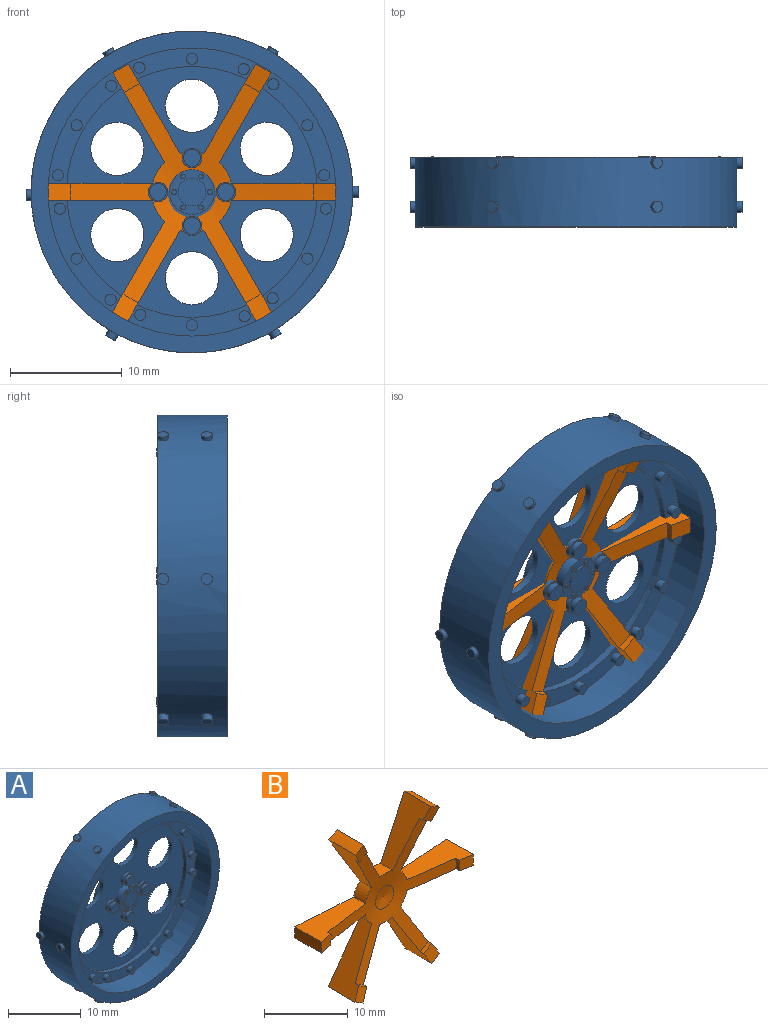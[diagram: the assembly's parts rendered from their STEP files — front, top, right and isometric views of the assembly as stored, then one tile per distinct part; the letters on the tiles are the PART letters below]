
ASSEMBLY  parts=2 mates=1
PART A: 117 faces, bbox 29.7x6.2x28.8 mm
  f0: cylinder r=14.39mm len=28.78mm, axis (0,1,0), area 551.2mm2, adj f1,f5,f87,f90,f92,f95,f97,f100
  f1: plane 28.78x28.78mm, normal (0,1,0), area 128.3mm2, adj f0,f3,f87,f88,f92,f93,f97,f98
  f2: plane 22.45x22.45mm, normal (0,-1,0), area 267.2mm2, adj f6,f9,f13,f17,f21,f25,f41,f42
  f3: cylinder r=12.89mm len=25.78mm, axis (0,1,0), area 137.7mm2, adj f1,f8
  f4: cylinder r=12.89mm len=25.78mm, axis (0,1,0), area 259.2mm2, adj f5,f7
  f5: plane 28.78x28.78mm, normal (0,-1,0), area 128.6mm2, adj f0,f4
  f6: cylinder r=11.22mm len=22.45mm, axis (0,1,0), area 45.8mm2, adj f2,f7
  f7: plane 25.78x25.78mm, normal (0,-1,0), area 112.1mm2, adj f4,f6,f47,f49,f51,f53,f55,f57
  f8: plane 25.78x25.78mm, normal (0,1,0), area 370.3mm2, adj f3,f41,f42,f43,f44,f45,f46,f84
  f9: cylinder r=0.88mm len=1.75mm, axis (0,1,0), area 2.7mm2, adj f2,f10
  f10: plane 1.75x1.75mm, normal (0,-1,0), area 0.6mm2, adj f9,f12
  f11: plane 1.5x1.5mm, normal (0,-1,0), area 1.8mm2, adj f12
  f12: cylinder r=0.75mm len=1.5mm, axis (0,1,0), area 2.8mm2, adj f10,f11
  f13: cylinder r=0.88mm len=1.75mm, axis (0,1,0), area 2.7mm2, adj f2,f14
  f14: plane 1.75x1.75mm, normal (0,-1,0), area 0.6mm2, adj f13,f16
  f15: plane 1.5x1.5mm, normal (0,-1,0), area 1.8mm2, adj f16
  f16: cylinder r=0.75mm len=1.5mm, axis (0,1,0), area 2.8mm2, adj f14,f15
  f17: cylinder r=0.88mm len=1.75mm, axis (0,1,0), area 2.7mm2, adj f2,f18
  f18: plane 1.75x1.75mm, normal (0,-1,0), area 0.6mm2, adj f17,f20
  f19: plane 1.5x1.5mm, normal (0,-1,0), area 1.8mm2, adj f20
  f20: cylinder r=0.75mm len=1.5mm, axis (0,1,0), area 2.8mm2, adj f18,f19
  f21: cylinder r=0.88mm len=1.75mm, axis (0,1,0), area 2.7mm2, adj f2,f22
  f22: plane 1.75x1.75mm, normal (0,-1,0), area 0.6mm2, adj f21,f24
  f23: plane 1.5x1.5mm, normal (0,-1,0), area 1.8mm2, adj f24
  f24: cylinder r=0.75mm len=1.5mm, axis (0,1,0), area 2.8mm2, adj f22,f23
  f25: cylinder r=2mm len=4mm, axis (0,1,0), area 11.3mm2, adj f2,f26
  f26: plane 4x4mm, normal (0,-1,0), area 6.8mm2, adj f25,f28,f30,f32,f34,f36,f38,f40
  f27: plane 0.44x0.44mm, normal (0,-1,0), area 0.1mm2, adj f28
  f28: cylinder r=0.22mm len=0.44mm, axis (0,1,0), area 0.3mm2, adj f26,f27
  f29: plane 0.44x0.44mm, normal (0,-1,0), area 0.1mm2, adj f30
  f30: cylinder r=0.22mm len=0.44mm, axis (0,1,0), area 0.3mm2, adj f26,f29
  f31: plane 0.44x0.44mm, normal (0,-1,0), area 0.1mm2, adj f32
  f32: cylinder r=0.22mm len=0.44mm, axis (0,1,0), area 0.3mm2, adj f26,f31
  f33: plane 0.44x0.44mm, normal (0,-1,0), area 0.1mm2, adj f34
  f34: cylinder r=0.22mm len=0.44mm, axis (0,1,0), area 0.3mm2, adj f26,f33
  f35: plane 0.44x0.44mm, normal (0,-1,0), area 0.1mm2, adj f36
  f36: cylinder r=0.22mm len=0.44mm, axis (0,1,0), area 0.3mm2, adj f26,f35
  f37: plane 2.5x2.5mm, normal (0,-1,0), area 4.9mm2, adj f38
  f38: cylinder r=1.25mm len=2.5mm, axis (0,1,0), area 1.6mm2, adj f26,f37
  f39: plane 0.44x0.44mm, normal (0,-1,0), area 0.1mm2, adj f40
  f40: cylinder r=0.22mm len=0.44mm, axis (0,1,0), area 0.3mm2, adj f26,f39
  f41: cylinder r=2.38mm len=4.75mm, axis (0,-1,0), area 9.7mm2, adj f2,f8
  f42: cylinder r=2.38mm len=4.75mm, axis (0,-1,0), area 9.7mm2, adj f2,f8
  f43: cylinder r=2.38mm len=4.75mm, axis (0,-1,0), area 9.7mm2, adj f2,f8
  f44: cylinder r=2.38mm len=4.75mm, axis (0,-1,0), area 9.7mm2, adj f2,f8
  f45: cylinder r=2.38mm len=4.75mm, axis (0,-1,0), area 9.7mm2, adj f2,f8
  f46: cylinder r=2.38mm len=4.75mm, axis (0,-1,0), area 9.7mm2, adj f2,f8
  f47: cylinder r=0.5mm len=1mm, axis (0,1,0), area 2.4mm2, adj f7,f48
  f48: plane 1x1mm, normal (0,-1,0), area 0.8mm2, adj f47
  f49: cylinder r=0.5mm len=1mm, axis (0,1,0), area 2.4mm2, adj f7,f50
  f50: plane 1x1mm, normal (0,-1,0), area 0.8mm2, adj f49
  f51: cylinder r=0.5mm len=1mm, axis (0,1,0), area 2.4mm2, adj f7,f52
  f52: plane 1x1mm, normal (0,-1,0), area 0.8mm2, adj f51
  f53: cylinder r=0.5mm len=1mm, axis (0,1,0), area 2.4mm2, adj f7,f54
  f54: plane 1x1mm, normal (0,-1,0), area 0.8mm2, adj f53
  f55: cylinder r=0.5mm len=1mm, axis (0,1,0), area 2.4mm2, adj f7,f56
  f56: plane 1x1mm, normal (0,-1,0), area 0.8mm2, adj f55
  f57: cylinder r=0.5mm len=1mm, axis (0,1,0), area 2.4mm2, adj f7,f58
  f58: plane 1x1mm, normal (0,-1,0), area 0.8mm2, adj f57
  f59: cylinder r=0.5mm len=1mm, axis (0,1,0), area 2.4mm2, adj f7,f60
  f60: plane 1x1mm, normal (0,-1,0), area 0.8mm2, adj f59
  f61: cylinder r=0.5mm len=1mm, axis (0,1,0), area 2.4mm2, adj f7,f62
  f62: plane 1x1mm, normal (0,-1,0), area 0.8mm2, adj f61
  f63: cylinder r=0.5mm len=1mm, axis (0,1,0), area 2.4mm2, adj f7,f64
  f64: plane 1x1mm, normal (0,-1,0), area 0.8mm2, adj f63
  f65: cylinder r=0.5mm len=1mm, axis (0,1,0), area 2.4mm2, adj f7,f66
  f66: plane 1x1mm, normal (0,-1,0), area 0.8mm2, adj f65
  f67: cylinder r=0.5mm len=1mm, axis (0,1,0), area 2.4mm2, adj f7,f68
  f68: plane 1x1mm, normal (0,-1,0), area 0.8mm2, adj f67
  f69: cylinder r=0.5mm len=1mm, axis (0,1,0), area 2.4mm2, adj f7,f70
  f70: plane 1x1mm, normal (0,-1,0), area 0.8mm2, adj f69
  f71: cylinder r=0.5mm len=1mm, axis (0,1,0), area 2.4mm2, adj f7,f72
  f72: plane 1x1mm, normal (0,-1,0), area 0.8mm2, adj f71
  f73: cylinder r=0.5mm len=1mm, axis (0,1,0), area 2.4mm2, adj f7,f74
  f74: plane 1x1mm, normal (0,-1,0), area 0.8mm2, adj f73
  f75: cylinder r=0.5mm len=1mm, axis (0,1,0), area 2.4mm2, adj f7,f76
  f76: plane 1x1mm, normal (0,-1,0), area 0.8mm2, adj f75
  f77: cylinder r=0.5mm len=1mm, axis (0,1,0), area 2.4mm2, adj f7,f78
  f78: plane 1x1mm, normal (0,-1,0), area 0.8mm2, adj f77
  f79: cylinder r=0.5mm len=1mm, axis (0,1,0), area 2.4mm2, adj f7,f80
  f80: plane 1x1mm, normal (0,-1,0), area 0.8mm2, adj f79
  f81: cylinder r=0.5mm len=1mm, axis (0,1,0), area 2.4mm2, adj f7,f82
  f82: plane 1x1mm, normal (0,-1,0), area 0.8mm2, adj f81
  f83: plane 7.6x7.6mm, normal (0,1,0), area 11.2mm2, adj f84,f85
  f84: cylinder r=3.8mm len=7.6mm, axis (0,-1,0), area 40.6mm2, adj f8,f83
  f85: cylinder r=3.3mm len=6.6mm, axis (0,-1,0), area 35.2mm2, adj f83,f86
  f86: plane 6.6x6.6mm, normal (0,1,0), area 34.2mm2, adj f85
  f87: cylinder r=0.5mm len=1mm, axis (-1,0,0), area 1.5mm2, adj f0,f1,f88,f89
  f88: plane 0.33x0.03mm, normal (-1,0,0), area 0mm2, adj f1,f87
  f89: plane 1x1mm, normal (1,0,0), area 0.8mm2, adj f87
  f90: cylinder r=0.5mm len=1mm, axis (-1,0,0), area 1.5mm2, adj f0,f91
  f91: plane 1x1mm, normal (1,0,0), area 0.8mm2, adj f90
  f92: cylinder r=0.5mm len=1.17mm, axis (-0.5,0,-0.87), area 1.2mm2, adj f0,f1,f93,f94
  f93: plane 0.29x0.17mm, normal (-0.5,0,-0.87), area 0mm2, adj f1,f92
  f94: plane 1x0.87mm, normal (0.5,0,0.87), area 0.8mm2, adj f92
  f95: cylinder r=0.5mm len=1.04mm, axis (-0.5,0,-0.87), area 1.1mm2, adj f0,f96
  f96: plane 1x0.87mm, normal (0.5,0,0.87), area 0.8mm2, adj f95
  f97: cylinder r=0.5mm len=1.17mm, axis (0.5,0,-0.87), area 1.2mm2, adj f0,f1,f98,f99
  f98: plane 0.29x0.17mm, normal (0.5,0,-0.87), area 0mm2, adj f1,f97
  f99: plane 1x0.87mm, normal (-0.5,0,0.87), area 0.8mm2, adj f97
  f100: cylinder r=0.5mm len=1.05mm, axis (0.5,0,-0.87), area 1.1mm2, adj f0,f101
  f101: plane 1x0.87mm, normal (-0.5,0,0.87), area 0.8mm2, adj f100
  f102: cylinder r=0.5mm len=1mm, axis (1,0,0), area 1.5mm2, adj f0,f1,f103,f104
  f103: plane 0.33x0.03mm, normal (1,0,0), area 0mm2, adj f1,f102
  f104: plane 1x1mm, normal (-1,0,0), area 0.8mm2, adj f102
  f105: cylinder r=0.5mm len=1mm, axis (1,0,0), area 1.5mm2, adj f0,f106
  f106: plane 1x1mm, normal (-1,0,0), area 0.8mm2, adj f105
  f107: cylinder r=0.5mm len=1.17mm, axis (0.5,0,0.87), area 1.8mm2, adj f0,f1,f108,f109
  f108: plane 0.29x0.17mm, normal (0.5,0,0.87), area 0mm2, adj f1,f107
  f109: plane 1x0.87mm, normal (-0.5,0,-0.87), area 0.8mm2, adj f107
  f110: cylinder r=0.5mm len=1.16mm, axis (0.5,0,0.87), area 1.8mm2, adj f0,f111
  f111: plane 1x0.87mm, normal (-0.5,0,-0.87), area 0.8mm2, adj f110
  f112: cylinder r=0.5mm len=1.17mm, axis (-0.5,0,0.87), area 1.8mm2, adj f0,f1,f113,f114
  f113: plane 0.29x0.17mm, normal (-0.5,0,0.87), area 0mm2, adj f1,f112
  f114: plane 1x0.87mm, normal (0.5,0,-0.87), area 0.8mm2, adj f112
  f115: cylinder r=0.5mm len=1.16mm, axis (-0.5,0,0.87), area 1.8mm2, adj f0,f116
  f116: plane 1x0.87mm, normal (0.5,0,-0.87), area 0.8mm2, adj f115
PART B: 40 faces, bbox 26.7x5.4x26.7 mm
  f0: cone r=1.56mm half-angle=82.5deg, axis (0,-1,0), area 120.4mm2, adj f14,f15,f16,f17,f18,f19,f20,f22
  f1: cone r=12.9mm half-angle=86.1deg, axis (0,1,0), area 151.1mm2, adj f2,f3,f4,f5,f6,f7,f21,f22
  f2: cylinder r=12.9mm len=4.52mm, axis (0,-1,0), area 7.2mm2, adj f1,f8,f23,f37
  f3: cylinder r=12.9mm len=4.52mm, axis (0,-1,0), area 7.2mm2, adj f1,f9,f34,f39
  f4: cylinder r=12.9mm len=4.52mm, axis (0,-1,0), area 7.2mm2, adj f1,f10,f31,f35
  f5: cylinder r=12.9mm len=4.52mm, axis (0,-1,0), area 7.2mm2, adj f1,f11,f28,f32
  f6: cylinder r=12.9mm len=4.52mm, axis (0,-1,0), area 7.2mm2, adj f1,f12,f25,f29
  f7: cylinder r=12.9mm len=4.52mm, axis (0,-1,0), area 7.2mm2, adj f1,f13,f22,f26
  f8: cone r=10.89mm half-angle=79.5deg, axis (0,-1,0), area 3.3mm2, adj f2,f14,f23,f37
  f9: cone r=10.89mm half-angle=79.5deg, axis (0,-1,0), area 3.3mm2, adj f3,f15,f34,f39
  f10: cone r=10.89mm half-angle=79.5deg, axis (0,-1,0), area 3.3mm2, adj f4,f16,f31,f35
  f11: cone r=10.89mm half-angle=79.5deg, axis (0,-1,0), area 3.3mm2, adj f5,f17,f28,f32
  f12: cone r=10.89mm half-angle=79.5deg, axis (0,-1,0), area 3.3mm2, adj f6,f18,f25,f29
  f13: cone r=10.89mm half-angle=79.5deg, axis (0,-1,0), area 3.3mm2, adj f7,f19,f22,f26
  f14: cylinder r=10.89mm len=1.39mm, axis (0,-1,0), area 0.9mm2, adj f0,f8,f23,f37
  f15: cylinder r=10.89mm len=1.39mm, axis (0,-1,0), area 0.9mm2, adj f0,f9,f34,f39
  f16: cylinder r=10.89mm len=1.6mm, axis (0,-1,0), area 0.9mm2, adj f0,f10,f31,f35
  f17: cylinder r=10.89mm len=1.38mm, axis (0,-1,0), area 0.9mm2, adj f0,f11,f28,f32
  f18: cylinder r=10.89mm len=1.38mm, axis (0,-1,0), area 0.9mm2, adj f0,f12,f25,f29
  f19: cylinder r=10.89mm len=1.6mm, axis (0,-1,0), area 0.9mm2, adj f0,f13,f22,f26
  f20: cone r=0mm half-angle=81.5deg, axis (0,-1,0), area 7.7mm2, adj f0
  f21: plane 3.11x3.11mm, normal (0,1,0), area 7.6mm2, adj f1
  f22: plane 10.22x5.39mm, normal (0,0,1), area 28.5mm2, adj f0,f1,f7,f13,f19,f24
  f23: plane 8.66x5.28mm, normal (0.87,0,-0.5), area 28.2mm2, adj f0,f1,f2,f8,f14,f24
  f24: cylinder r=3.6mm len=2mm, axis (0,1,0), area 4.3mm2, adj f0,f1,f22,f23
  f25: plane 9.07x5.6mm, normal (0.87,0,0.5), area 28.7mm2, adj f0,f1,f6,f12,f18,f27
  f26: plane 10x5.15mm, normal (0,0,-1), area 28.5mm2, adj f0,f1,f7,f13,f19,f27
  f27: cylinder r=3.6mm len=1.98mm, axis (0,1,0), area 4.2mm2, adj f0,f1,f25,f26
  f28: plane 8.95x5.48mm, normal (0.87,0,-0.5), area 28.7mm2, adj f0,f1,f5,f11,f17,f30
  f29: plane 8.95x5.48mm, normal (-0.87,0,-0.5), area 28.7mm2, adj f0,f1,f6,f12,f18,f30
  f30: cylinder r=3.6mm len=2.12mm, axis (0,1,0), area 4.2mm2, adj f0,f1,f28,f29
  f31: plane 10x5.15mm, normal (0,0,-1), area 28.5mm2, adj f0,f1,f4,f10,f16,f33
  f32: plane 9.07x5.6mm, normal (-0.87,0,0.5), area 28.7mm2, adj f0,f1,f5,f11,f17,f33
  f33: cylinder r=3.6mm len=1.98mm, axis (0,1,0), area 4.2mm2, adj f0,f1,f31,f32
  f34: plane 8.66x5.28mm, normal (-0.87,0,-0.5), area 28.2mm2, adj f0,f1,f3,f9,f15,f36
  f35: plane 10.22x5.39mm, normal (0,0,1), area 28.5mm2, adj f0,f1,f4,f10,f16,f36
  f36: cylinder r=3.6mm len=2mm, axis (0,1,0), area 4.3mm2, adj f0,f1,f34,f35
  f37: plane 8.77x5.39mm, normal (-0.87,0,0.5), area 28.2mm2, adj f0,f1,f2,f8,f14,f38
  f38: cylinder r=3.6mm len=2.12mm, axis (0,1,0), area 4.3mm2, adj f0,f1,f37,f39
  f39: plane 8.77x5.39mm, normal (0.87,0,0.5), area 28.2mm2, adj f0,f1,f3,f9,f15,f38
PLACE A t=(0,-0.29,0)mm
PLACE B at identity
MATE fastened A.f84 <-> B.f0  axis (0,1,0) through (0,-0.29,-1.56)mm
